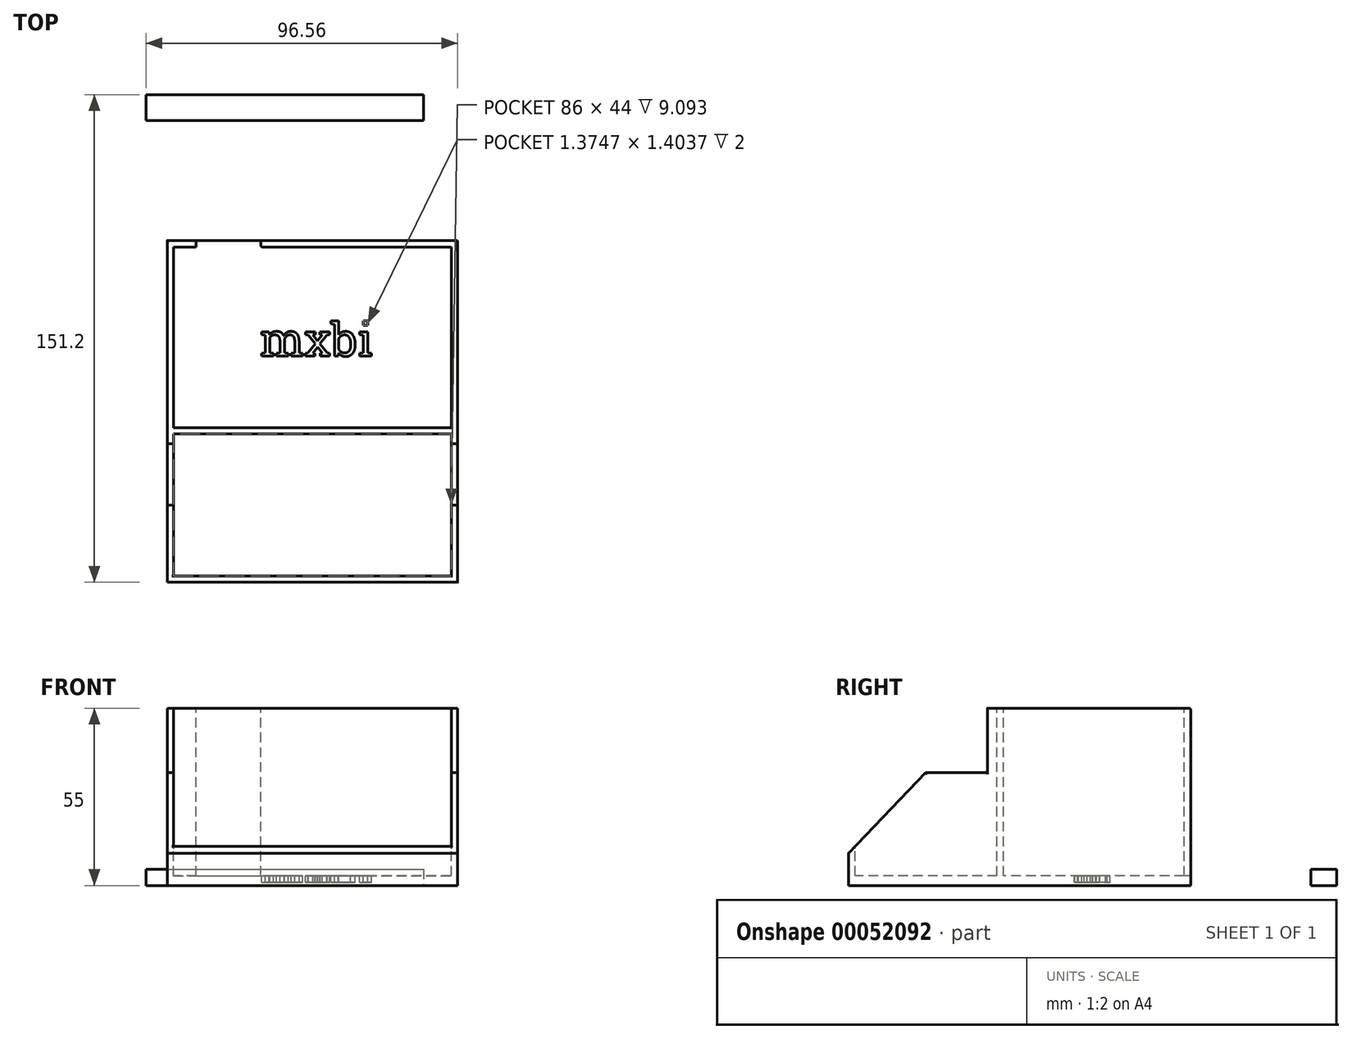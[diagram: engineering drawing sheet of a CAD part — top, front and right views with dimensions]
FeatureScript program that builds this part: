
annotation { "Feature Type Name" : "Feature", "Feature Type Description" : "" }
export const myFeature = defineFeature(function(context is Context, id is Id, definition is map)
    precondition{}
    {
        {
            var Q0;
            Q0=qCreatedBy(makeId("Top.planeOp"),FACE);
            var sketch = newSketch(context, id + "F0", { "sketchPlane" : qUnion([Q0])});
            skLineSegment(sketch, "E0.bottom", {"start": v(0, 0) * mm, "end": v(90, 0) * mm});
            skLineSegment(sketch, "E0.top", {"start": v(0, -106) * mm, "end": v(90, -106) * mm});
            skLineSegment(sketch, "E0.left", {"start": v(0, 0) * mm, "end": v(0, -106) * mm});
            skLineSegment(sketch, "E0.right", {"start": v(90, 0) * mm, "end": v(90, -106) * mm});
            skSolve(sketch);
        }
        {
            var Q0;
            Q0=makeQuery(id+"F0.imprint","IMPRINT",FACE,{"disambiguationData":[TD([[makeQuery(id+"F0.imprint","IMPRINT",EDGE,{"derivedFrom":sQuery(id+"F0.wireOp",EDGE,"E0.bottom")}),-1.0]])]});
            extrude(context, id + "F1", {"entities" : qUnion([Q0]), "depth" : 55 * mm});
        }
        {
            var Q0;
            Q0=makeQuery(id+"F1.opExtrude","CAP_FACE",FACE,{"disambiguationData":[OSD([sQuery(id+"F0.wireOp",EDGE,"E0.bottom"),sQuery(id+"F0.wireOp",EDGE,"E0.top"),sQuery(id+"F0.wireOp",EDGE,"E0.left"),sQuery(id+"F0.wireOp",EDGE,"E0.right")])],"isStart":false});
            var sketch = newSketch(context, id + "F2", { "sketchPlane" : qUnion([Q0])});
            skLineSegment(sketch, "E1", {"start": v(2, 0) * mm, "end": v(2, -106) * mm, "construction": true});
            skLineSegment(sketch, "E2", {"start": v(88, 0) * mm, "end": v(88, -106) * mm, "construction": true});
            skLineSegment(sketch, "E3", {"start": v(0, -2) * mm, "end": v(90, -2) * mm, "construction": true});
            skLineSegment(sketch, "E4", {"start": v(0, -58) * mm, "end": v(90, -58) * mm, "construction": true});
            skLineSegment(sketch, "E5", {"start": v(2, -2) * mm, "end": v(2, -58) * mm});
            skLineSegment(sketch, "E6", {"start": v(2, -58) * mm, "end": v(88, -58) * mm});
            skLineSegment(sketch, "E7", {"start": v(88, -58) * mm, "end": v(88, -2) * mm});
            skLineSegment(sketch, "E8", {"start": v(88, -2) * mm, "end": v(2, -2) * mm});
            skLineSegment(sketch, "E9", {"start": v(0, -60) * mm, "end": v(90, -60) * mm, "construction": true});
            skLineSegment(sketch, "E10", {"start": v(0, -104) * mm, "end": v(90, -104) * mm, "construction": true});
            skLineSegment(sketch, "E11", {"start": v(2, -60) * mm, "end": v(2, -104) * mm});
            skLineSegment(sketch, "E12", {"start": v(2, -104) * mm, "end": v(88, -104) * mm});
            skLineSegment(sketch, "E13", {"start": v(88, -104) * mm, "end": v(88, -60) * mm});
            skLineSegment(sketch, "E14", {"start": v(88, -60) * mm, "end": v(2, -60) * mm});
            skSolve(sketch);
        }
        {
            var Q0;
            Q0 = qSketchRegion(id + "F2", true);
            extrude(context, id + "F3", {"entities" : qUnion([Q0]), "operationType" : NewBodyOperationType.REMOVE, "oppositeDirection" : true, "depth" : 52 * mm});
        }
        {
            var Q0;
            Q0=makeQuery(id+"F1.opExtrude","SWEPT_FACE",FACE,{"disambiguationData":[OSD([sQuery(id+"F0.wireOp",EDGE,"E0.left")])]});
            var sketch = newSketch(context, id + "F4", { "sketchPlane" : qUnion([Q0])});
            skLineSegment(sketch, "E15", {"start": v(63, 55) * mm, "end": v(106, 10) * mm, "construction": true});
            skLineSegment(sketch, "E16", {"start": v(0, 35) * mm, "end": v(106, 35) * mm, "construction": true});
            skLineSegment(sketch, "E17", {"start": v(63, 55) * mm, "end": v(63, 35) * mm});
            skLineSegment(sketch, "E18", {"start": v(63, 35) * mm, "end": v(82.11, 35) * mm});
            skLineSegment(sketch, "E19", {"start": v(82.11, 35) * mm, "end": v(106, 10) * mm});
            skSolve(sketch);
        }
        {
            var Q0;
            {var subQ5=sQuery(id+"F4.wireOp",EDGE,"E17");Q0=makeQuery(id+"F4.imprint","IMPRINT",FACE,{"disambiguationData":[TD([[makeQuery(id+"F4.imprint","IMPRINT",EDGE,{"derivedFrom":subQ5}),1.0]])]});}
            extrude(context, id + "F5", {"entities" : qUnion([Q0]), "operationType" : NewBodyOperationType.REMOVE, "oppositeDirection" : true, "depth" : 100 * mm});
        }
        {
            var Q0;
            Q0=makeQuery(id+"F1.opExtrude","CAP_FACE",FACE,{"disambiguationData":[OSD([sQuery(id+"F0.wireOp",EDGE,"E0.bottom"),sQuery(id+"F0.wireOp",EDGE,"E0.top"),sQuery(id+"F0.wireOp",EDGE,"E0.left"),sQuery(id+"F0.wireOp",EDGE,"E0.right")])],"isStart":false});
            var sketch = newSketch(context, id + "F6", { "sketchPlane" : qUnion([Q0])});
            skLineSegment(sketch, "E20", {"start": v(9, 0) * mm, "end": v(9, -2) * mm});
            skLineSegment(sketch, "E21", {"start": v(29, 0) * mm, "end": v(29, -2) * mm});
            skSolve(sketch);
        }
        {
            var Q0;
            {var subQ0=sQuery(id+"F6.wireOp",EDGE,"E20");Q0=makeQuery(id+"F6.imprint","IMPRINT",FACE,{"disambiguationData":[TD([[makeQuery(id+"F6.imprint","IMPRINT",EDGE,{"derivedFrom":subQ0}),1.0]])]});}
            extrude(context, id + "F7", {"entities" : qUnion([Q0]), "operationType" : NewBodyOperationType.REMOVE, "oppositeDirection" : true, "depth" : 52 * mm});
        }
        {
            var Q0;
            Q0=makeQuery(id+"F5.boolean.opBoolean","MERGE",EDGE,{"derivedFrom":[makeQuery(id+"F3.boolean.opBoolean","COPY",EDGE,{"derivedFrom":makeQuery(id+"F3.opExtrude","CAP_EDGE",EDGE,{"disambiguationData":[OSD([sQuery(id+"F2.wireOp",EDGE,"E14")])],"isStart":true})}),makeQuery(id+"F5.opExtrude","SWEPT_EDGE",EDGE,{"disambiguationData":[OSD([sQuery(id+"F0.wireOp",EDGE,"E0.left"),sQuery(id+"F4.wireOp",EDGE,"E17")])]})]});
            var Q1;
            Q1=makeQuery(id+"F1.opExtrude","CAP_EDGE",EDGE,{"disambiguationData":[OSD([sQuery(id+"F0.wireOp",EDGE,"E0.left")])],"isStart":false});
            var Q2;
            Q2=makeQuery(id+"F3.boolean.opBoolean","COPY",EDGE,{"derivedFrom":makeQuery(id+"F3.opExtrude","CAP_EDGE",EDGE,{"disambiguationData":[OSD([sQuery(id+"F2.wireOp",EDGE,"E5")])],"isStart":true})});
            var Q3;
            Q3=makeQuery(id+"F3.boolean.opBoolean","COPY",EDGE,{"derivedFrom":makeQuery(id+"F3.opExtrude","CAP_EDGE",EDGE,{"disambiguationData":[OSD([sQuery(id+"F2.wireOp",EDGE,"E6")])],"isStart":true})});
            var Q4;
            Q4=makeQuery(id+"F3.boolean.opBoolean","COPY",EDGE,{"derivedFrom":makeQuery(id+"F3.opExtrude","CAP_EDGE",EDGE,{"disambiguationData":[OSD([sQuery(id+"F2.wireOp",EDGE,"E7")])],"isStart":true})});
            var Q5;
            Q5=makeQuery(id+"F1.opExtrude","CAP_EDGE",EDGE,{"disambiguationData":[OSD([sQuery(id+"F0.wireOp",EDGE,"E0.right")])],"isStart":false});
            var Q6;
            {var subQ0=sQuery(id+"F2.wireOp",EDGE,"E8");Q6=makeQuery(id+"F7.boolean.opBoolean","SPLIT",EDGE,{"disambiguationData":[TD([makeQuery(id+"F3.boolean.opBoolean","COPY",FACE,{"derivedFrom":makeQuery(id+"F3.opExtrude","SWEPT_FACE",FACE,{"disambiguationData":[OSD([sQuery(id+"F2.wireOp",EDGE,"E5")])]})})])],"derivedFrom":makeQuery(id+"F3.boolean.opBoolean","COPY",EDGE,{"derivedFrom":makeQuery(id+"F3.opExtrude","CAP_EDGE",EDGE,{"disambiguationData":[OSD([subQ0])],"isStart":true})})});}
            var Q7;
            Q7=makeQuery(id+"F7.boolean.opBoolean","COPY",EDGE,{"derivedFrom":makeQuery(id+"F7.opExtrude","CAP_EDGE",EDGE,{"disambiguationData":[OSD([sQuery(id+"F6.wireOp",EDGE,"E20")])],"isStart":true})});
            var Q8;
            {var subQ0=sQuery(id+"F0.wireOp",EDGE,"E0.bottom");var subQ1=sQuery(id+"F0.wireOp",EDGE,"E0.left");Q8=makeQuery(id+"F7.boolean.opBoolean","SPLIT",EDGE,{"disambiguationData":[TD([makeQuery(id+"F1.opExtrude","SWEPT_FACE",FACE,{"disambiguationData":[OSD([subQ1])]})])],"derivedFrom":makeQuery(id+"F1.opExtrude","CAP_EDGE",EDGE,{"disambiguationData":[OSD([subQ0])],"isStart":false})});}
            var Q9;
            {var subQ0=sQuery(id+"F2.wireOp",EDGE,"E8");Q9=makeQuery(id+"F7.boolean.opBoolean","SPLIT",EDGE,{"disambiguationData":[TD([makeQuery(id+"F3.boolean.opBoolean","COPY",FACE,{"derivedFrom":makeQuery(id+"F3.opExtrude","SWEPT_FACE",FACE,{"disambiguationData":[OSD([sQuery(id+"F2.wireOp",EDGE,"E7")])]})})])],"derivedFrom":makeQuery(id+"F3.boolean.opBoolean","COPY",EDGE,{"derivedFrom":makeQuery(id+"F3.opExtrude","CAP_EDGE",EDGE,{"disambiguationData":[OSD([subQ0])],"isStart":true})})});}
            var Q10;
            {var subQ0=sQuery(id+"F0.wireOp",EDGE,"E0.bottom");var subQ1=sQuery(id+"F0.wireOp",EDGE,"E0.right");Q10=makeQuery(id+"F7.boolean.opBoolean","SPLIT",EDGE,{"disambiguationData":[TD([makeQuery(id+"F1.opExtrude","SWEPT_FACE",FACE,{"disambiguationData":[OSD([subQ1])]})])],"derivedFrom":makeQuery(id+"F1.opExtrude","CAP_EDGE",EDGE,{"disambiguationData":[OSD([subQ0])],"isStart":false})});}
            var Q11;
            Q11=makeQuery(id+"F7.boolean.opBoolean","COPY",EDGE,{"derivedFrom":makeQuery(id+"F7.opExtrude","CAP_EDGE",EDGE,{"disambiguationData":[OSD([sQuery(id+"F6.wireOp",EDGE,"E21")])],"isStart":true})});
            var Q12;
            Q12=makeQuery(id+"F7.boolean.opBoolean","COPY",EDGE,{"derivedFrom":makeQuery(id+"F7.opExtrude","SWEPT_EDGE",EDGE,{"disambiguationData":[OSD([sQuery(id+"F0.wireOp",EDGE,"E0.bottom"),sQuery(id+"F6.wireOp",EDGE,"E21")])]})});
            var Q13;
            Q13=makeQuery(id+"F7.boolean.opBoolean","COPY",EDGE,{"derivedFrom":makeQuery(id+"F7.opExtrude","SWEPT_EDGE",EDGE,{"disambiguationData":[OSD([sQuery(id+"F2.wireOp",EDGE,"E8"),sQuery(id+"F6.wireOp",EDGE,"E21")])]})});
            var Q14;
            Q14=makeQuery(id+"F7.boolean.opBoolean","COPY",EDGE,{"derivedFrom":makeQuery(id+"F7.opExtrude","SWEPT_EDGE",EDGE,{"disambiguationData":[OSD([sQuery(id+"F2.wireOp",EDGE,"E8"),sQuery(id+"F6.wireOp",EDGE,"E20")])]})});
            var Q15;
            Q15=makeQuery(id+"F7.boolean.opBoolean","COPY",EDGE,{"derivedFrom":makeQuery(id+"F7.opExtrude","SWEPT_EDGE",EDGE,{"disambiguationData":[OSD([sQuery(id+"F0.wireOp",EDGE,"E0.bottom"),sQuery(id+"F6.wireOp",EDGE,"E20")])]})});
            fillet(context, id + "F8", {"entities" : qUnion([Q0, Q1, Q2, Q3, Q4, Q5, Q6, Q7, Q8, Q9, Q10, Q11, Q12, Q13, Q14, Q15]), "radius" : 0.5 * mm, "tangentPropagation" : true, "allowEdgeOverflow" : false});
        }
        {
            var Q0;
            Q0=makeQuery(id+"F5.boolean.opBoolean","COPY",EDGE,{"derivedFrom":makeQuery(id+"F5.opExtrude","SWEPT_EDGE",EDGE,{"disambiguationData":[OSD([sQuery(id+"F0.wireOp",EDGE,"E0.top"),sQuery(id+"F0.wireOp",EDGE,"E0.left"),sQuery(id+"F4.wireOp",EDGE,"E19")])]})});
            var Q1;
            Q1=makeQuery(id+"F5.boolean.opBoolean","INTERSECT",EDGE,{"derivedFrom":[makeQuery(id+"F1.opExtrude","SWEPT_FACE",FACE,{"disambiguationData":[OSD([sQuery(id+"F0.wireOp",EDGE,"E0.right")])]}),makeQuery(id+"F5.opExtrude","SWEPT_FACE",FACE,{"disambiguationData":[OSD([sQuery(id+"F4.wireOp",EDGE,"E19")])]})]});
            var Q2;
            Q2=makeQuery(id+"F5.boolean.opBoolean","INTERSECT",EDGE,{"derivedFrom":[makeQuery(id+"F1.opExtrude","SWEPT_FACE",FACE,{"disambiguationData":[OSD([sQuery(id+"F0.wireOp",EDGE,"E0.right")])]}),makeQuery(id+"F5.opExtrude","SWEPT_FACE",FACE,{"disambiguationData":[OSD([sQuery(id+"F4.wireOp",EDGE,"E18")])]})]});
            var Q3;
            Q3=makeQuery(id+"F5.boolean.opBoolean","INTERSECT",EDGE,{"derivedFrom":[makeQuery(id+"F3.boolean.opBoolean","COPY",FACE,{"derivedFrom":makeQuery(id+"F3.opExtrude","SWEPT_FACE",FACE,{"disambiguationData":[OSD([sQuery(id+"F2.wireOp",EDGE,"E13")])]})}),makeQuery(id+"F5.opExtrude","SWEPT_FACE",FACE,{"disambiguationData":[OSD([sQuery(id+"F4.wireOp",EDGE,"E19")])]})]});
            var Q4;
            Q4=makeQuery(id+"F5.boolean.opBoolean","INTERSECT",EDGE,{"derivedFrom":[makeQuery(id+"F3.boolean.opBoolean","COPY",FACE,{"derivedFrom":makeQuery(id+"F3.opExtrude","SWEPT_FACE",FACE,{"disambiguationData":[OSD([sQuery(id+"F2.wireOp",EDGE,"E13")])]})}),makeQuery(id+"F5.opExtrude","SWEPT_FACE",FACE,{"disambiguationData":[OSD([sQuery(id+"F4.wireOp",EDGE,"E18")])]})]});
            var Q5;
            Q5=makeQuery(id+"F5.boolean.opBoolean","COPY",EDGE,{"derivedFrom":makeQuery(id+"F5.opExtrude","CAP_EDGE",EDGE,{"disambiguationData":[OSD([sQuery(id+"F4.wireOp",EDGE,"E19")])],"isStart":true})});
            var Q6;
            Q6=makeQuery(id+"F5.boolean.opBoolean","INTERSECT",EDGE,{"derivedFrom":[makeQuery(id+"F3.boolean.opBoolean","COPY",FACE,{"derivedFrom":makeQuery(id+"F3.opExtrude","SWEPT_FACE",FACE,{"disambiguationData":[OSD([sQuery(id+"F2.wireOp",EDGE,"E11")])]})}),makeQuery(id+"F5.opExtrude","SWEPT_FACE",FACE,{"disambiguationData":[OSD([sQuery(id+"F4.wireOp",EDGE,"E19")])]})]});
            var Q7;
            Q7=makeQuery(id+"F5.boolean.opBoolean","COPY",EDGE,{"derivedFrom":makeQuery(id+"F5.opExtrude","CAP_EDGE",EDGE,{"disambiguationData":[OSD([sQuery(id+"F4.wireOp",EDGE,"E18")])],"isStart":true})});
            var Q8;
            Q8=makeQuery(id+"F5.boolean.opBoolean","INTERSECT",EDGE,{"derivedFrom":[makeQuery(id+"F3.boolean.opBoolean","COPY",FACE,{"derivedFrom":makeQuery(id+"F3.opExtrude","SWEPT_FACE",FACE,{"disambiguationData":[OSD([sQuery(id+"F2.wireOp",EDGE,"E11")])]})}),makeQuery(id+"F5.opExtrude","SWEPT_FACE",FACE,{"disambiguationData":[OSD([sQuery(id+"F4.wireOp",EDGE,"E18")])]})]});
            fillet(context, id + "F9", {"entities" : qUnion([Q0, Q1, Q2, Q3, Q4, Q5, Q6, Q7, Q8]), "radius" : 0.5 * mm, "tangentPropagation" : true, "allowEdgeOverflow" : false});
        }
        {
            var Q0;
            Q0=qCreatedBy(makeId("Top.planeOp"),FACE);
            var sketch = newSketch(context, id + "F10", { "sketchPlane" : qUnion([Q0])});
            skLineSegment(sketch, "E22.bottom", {"start": v(-6.56, 37.2) * mm, "end": v(79.44, 37.2) * mm});
            skLineSegment(sketch, "E22.top", {"start": v(-6.56, 45.2) * mm, "end": v(79.44, 45.2) * mm});
            skLineSegment(sketch, "E22.left", {"start": v(-6.56, 37.2) * mm, "end": v(-6.56, 45.2) * mm});
            skLineSegment(sketch, "E22.right", {"start": v(79.44, 37.2) * mm, "end": v(79.44, 45.2) * mm});
            skSolve(sketch);
        }
        {
            var Q0;
            Q0=makeQuery(id+"F10.imprint","IMPRINT",FACE,{"disambiguationData":[TD([[makeQuery(id+"F10.imprint","IMPRINT",EDGE,{"derivedFrom":sQuery(id+"F10.wireOp",EDGE,"E22.bottom")}),1.0]])]});
            extrude(context, id + "F11", {"entities" : qUnion([Q0]), "depth" : 5 * mm});
        }
        {
            var Q0;
            {var subQ0=sQuery(id+"F2.wireOp",EDGE,"E8");Q0=makeQuery(id+"F7.boolean.opBoolean","MERGE",FACE,{"derivedFrom":[makeQuery(id+"F3.boolean.opBoolean","COPY",FACE,{"derivedFrom":makeQuery(id+"F3.opExtrude","CAP_FACE",FACE,{"disambiguationData":[OSD([sQuery(id+"F2.wireOp",EDGE,"E5"),sQuery(id+"F2.wireOp",EDGE,"E6"),sQuery(id+"F2.wireOp",EDGE,"E7"),subQ0])],"isStart":false})}),makeQuery(id+"F7.opExtrude","CAP_FACE",FACE,{"disambiguationData":[OSD([sQuery(id+"F0.wireOp",EDGE,"E0.bottom"),subQ0,sQuery(id+"F6.wireOp",EDGE,"E20"),sQuery(id+"F6.wireOp",EDGE,"E21")])],"isStart":false})]});}
            var sketch = newSketch(context, id + "F12", { "sketchPlane" : qUnion([Q0])});
            skLineSegment(sketch, "E23", {"start": v(2, -2) * mm, "end": v(88, -2) * mm, "construction": true});
            skLineSegment(sketch, "E24", {"start": v(45, -2) * mm, "end": v(45, -58) * mm, "construction": true});
            skLineSegment(sketch, "E25", {"start": v(2, -30) * mm, "end": v(88, -30) * mm, "construction": true});
            skText(sketch, "E26", { "text": "mxbi", "fontName": "RobotoSlab-Regular.ttf"});
            const initialGuessF12  = {"E26": [0.02888, -0.03585, 1, 0, 0.0103]};
            skSetInitialGuess(sketch, initialGuessF12);
            skSolve(sketch);
        }
        {
            var Q0;
            Q0 = qSketchRegion(id + "F12", true);
            extrude(context, id + "F13", {"entities" : qUnion([Q0]), "operationType" : NewBodyOperationType.REMOVE, "oppositeDirection" : true, "depth" : 2 * mm});
        }
    });
